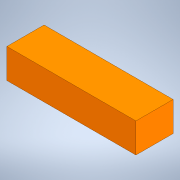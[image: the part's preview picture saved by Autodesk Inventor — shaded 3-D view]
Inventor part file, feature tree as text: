
AUTODESK INVENTOR PART (.ipt)
format: ipt  version: 2020.2 (Build 242310000, 310)  size: 96,768 bytes
history: native  units: mm
features: extrude x1, sketch x1
ambient origin geometry x8: Origin, YZ Plane, XZ Plane, XY Plane, X Axis, Y Axis, Z Axis, Center Point
bodies: Solid1 (feature_tree)
feature tree (2):
  extrude  "Extrusion1"  Depth=34.0mm
  sketch  "Sketch1"  dims[d0=118.0mm d1=34.0mm d2=27.0mm d3=0.0mm]
